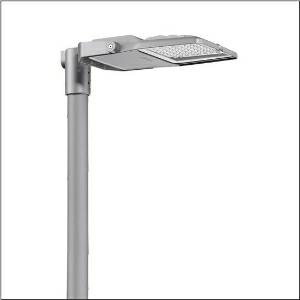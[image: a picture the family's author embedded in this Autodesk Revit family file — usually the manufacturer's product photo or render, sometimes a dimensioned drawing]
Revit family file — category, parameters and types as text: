
# Revit family: floodlight_fl_21_iq_mini___pl61_5xa7772c4c3a_2e37
name_source: partatom
category: Lighting Fixtures
units: mm (PartAtom-declared; Revit-internal decimal feet)

## family parameters
Cut with Voids When Loaded = No
Host = Face
Light Source = No
Part Type = Normal
Room Calculation Point = No
Round Connector Dimension = Use Diameter
Shared = No

## types (1)
- --- (1 x LED, 12490 lm, 87.2 W, 4000K)
    Apparent Load = 87 VA
    CIE Flux Codes = 33 65 98 100 100
    Color Rendering = 70
    Color Temperature = 4000K
    Default Elevation = 1800 mm
    Description = Floodlight FL 21 iQ mini, floodlight, primary light control with lens, of PMMA, primary optical cover: protective disc, of toughened safety glass, transparent, light distribution: PL61, light emission: direct distribution, installation type: surface-mounted, LED, High Power LED, rated luminous flux: 12.490lm, luminous efficacy: 143lm/W, light colour: 740, colour temperature: 4000K, control gear: iQ Street-Remote/DALI, control: Auto-Match, Temp-Guard, Night-Set, Smart-Wire, Desk-Remote (wireless, voltage-free reading and setting of iQ features in the workshop via application-optimized NFC function/RFID function), optimised constant luminous flux control (CLO 2.0), Light-Fading, Lumen-Switch, with terminal, 6-pole, mains connection: 220..240V, AC, 50/60Hz, start of lifetime: 87W, end of service life: 92W, reduction: 40W, luminaire housing, of diecast aluminium, powder-coated, Siteco® metallic grey (DB 702S), corrosivity category C5 mid according to DIN EN ISO 12944, suitable for swimming pools, chlorine-resistant, sealing non-destructively replaceable, please order mast flange separately, mast bracket, of steel, galvanised, powder-coated, protection rating (complete): IP66, insulation class (complete): insulation class II (safety insulation), certification: CE, ENEC, VDE, protection symbol: D, impact resistance: IK08, permissible operating ambient temperature: -40..+40°C, permissible operating ambient temperature for outdoor applications: -40..+50°C, standard: DIN EN 12944, LABS conformity tested according to VDMA 24364:2018-05, packaging unit: 1 piece

Light Distribution: PL61
    Height = 70 mm
    Lamp = 1 x LED
    Lamp Light Flux = 12490 lm
    Lamp Power = 87.2 W
    Lamp count = 1
    Length = 485 mm
    Luminous efficacy = 143 lm/W
    Manufacturer = Siteco
    ModVariant = No
    Model = 5XA7772C4C3A
    Number of Poles = 1
    OnlyDefault = Yes
    Power Factor = 1
    Product Name = Floodlight FL 21 iQ mini | PL61
    Product group = floodlight | pylon annexe
    ProductGroupID = 6201
    Protection Class = Protection class II
    Protection Degree = IP 66
    RLX_Detail_Level = 1
    RLX_Emergency_Light_Flux = 0 lm
    RLX_Emergency_Type = 0
    RLX_Emergency_Type_DB = No
    RlxData = <blob elided: 101389 chars, md5=c805b794>
    Socket = socket
    Standby Power = 0 W
    System Light Flux = 12490 lm
    System Power = 87 W
    Type Comments = factory setting: luminous flux: 100 % | dim-lin: 254 | 456 mA
    Type Image = l_1007125.jpg
    URL = http://relux.com
    VarID = @adj_194373
    Voltage = 0 V
    Weight = 0.00 kg
    Width = 337 mm

## geometry (parser evidence)
native form markers: Blend x4, Sweep x10
no freeform markers — native parametric forms only
